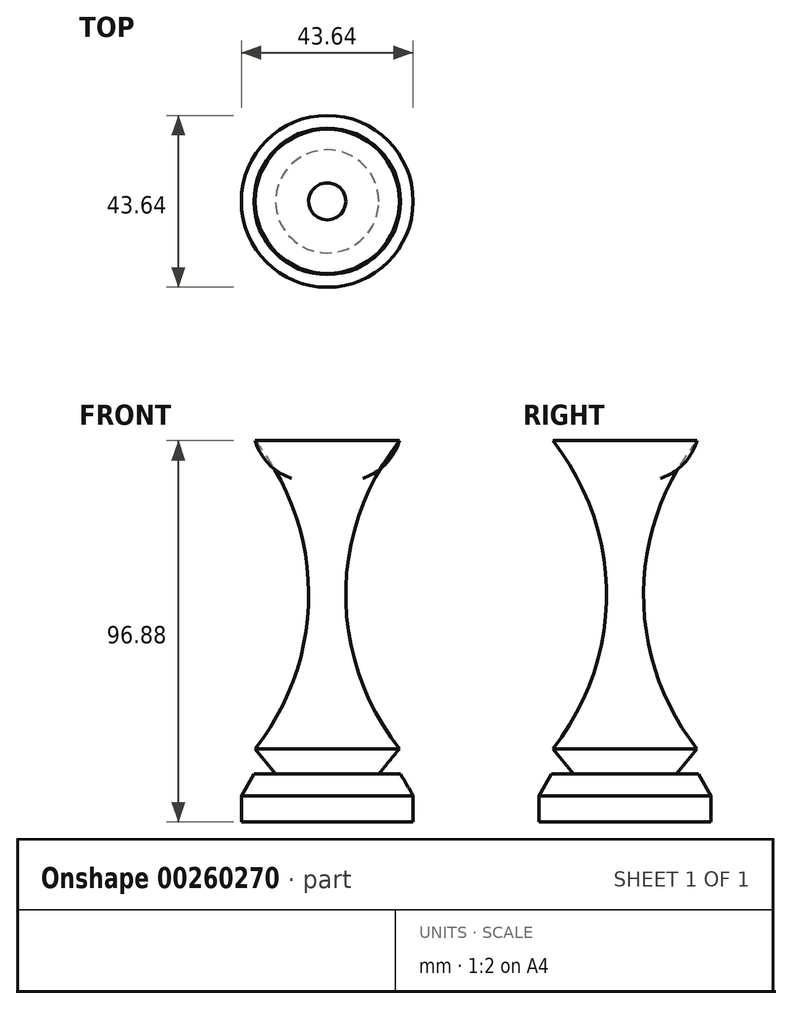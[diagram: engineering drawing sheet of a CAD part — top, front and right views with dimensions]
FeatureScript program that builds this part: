
annotation { "Feature Type Name" : "Feature", "Feature Type Description" : "" }
export const myFeature = defineFeature(function(context is Context, id is Id, definition is map)
    precondition{}
    {
        {
            var Q0;
            Q0=qCreatedBy(makeId("Front.planeOp"),FACE);
            var sketch = newSketch(context, id + "F0", { "sketchPlane" : qUnion([Q0])});
            skLineSegment(sketch, "E0", {"start": v(0, 75.94) * mm, "end": v(0, -76.23) * mm, "construction": true});
            skArc(sketch, "E1", {"start": v(0, 71.28) * mm, "mid": v(-14.54, 67.96) * mm, "end": v(-18.33, 53.53) * mm});
            skArc(sketch, "E2", {"start": v(-18.33, -24.73) * mm, "mid": v(-4.71, 14.4) * mm, "end": v(-18.33, 53.53) * mm});
            skLineSegment(sketch, "E3", {"start": v(-18.33, -24.73) * mm, "end": v(-13.1, -31.13) * mm});
            skLineSegment(sketch, "E4", {"start": v(-13.1, -31.13) * mm, "end": v(-18.62, -31.13) * mm});
            skLineSegment(sketch, "E5", {"start": v(-18.62, -31.13) * mm, "end": v(-21.82, -36.66) * mm});
            skLineSegment(sketch, "E6", {"start": v(-21.82, -36.66) * mm, "end": v(-21.82, -43.35) * mm});
            skLineSegment(sketch, "E7", {"start": v(-21.82, -43.35) * mm, "end": v(0, -43.35) * mm});
            skLineSegment(sketch, "E8", {"start": v(0, 71.28) * mm, "end": v(0, -43.35) * mm});
            skSolve(sketch);
        }
        {
            var Q0;
            Q0 = qSketchRegion(id + "F0", true);
            var Q1;
            Q1=sQuery(id+"F0.wireOp",EDGE,"E8");
            revolve(context, id + "F1", {"entities" : qUnion([Q0]), "axis" : qUnion([Q1]), "revolveType" : RevolveType.FULL});
        }
    });
